# Revit family: Gira_220303
name_source: partatom
category: Elektroinstallationen
revit_build: Autodesk Revit 2017 (Build: 20160225_1515(x64)
units: mm (PartAtom-declared; Revit-internal decimal feet)

## family parameters
Basisbauteil = Fläche
Beim Laden mit Abzugskörper schneiden = Nein
Bemaßung runder Anschluss = Durchmesser verwenden
Beschriftungsausrichtung beibehalten = Nein
Gemeinsam genutzt = Nein
Raumberechnungspunkt = Nein
Teiletyp = Normal

## types (2) — shared parameters
Acoustic signal = Ja
Analogue input = Nein
BIM = https://media.stage.bim.site und Tasten.rfa
Beschreibung = Rock.set 3g insc. Sys55 PWl,Rocker set, 3-gang inscribable,System 55,pure white glossy (lacquered),Notes :,- Inscribable rocker sets and rocker sets with inscription space can be provided with a customised inscription. The order is processed by the wholesaler specified during the rockers' order process.,- Inscribable rocker sets and rocker sets without inscription space are made of metal, which can lead to impairments to the range in wireless applications.,- This product can only be ordered via the Gira Inscription Service.,- Professional labelling with the Gira Inscription Service www.marking.gira.com.
Bus connection included = Nein
Bus system KNX = Ja
Bus system KNX radio = Nein
Bus system LON = Nein
Bus system Powernet = Nein
Bus system radio frequent = Nein
Colour = White
Data sheet = https://katalog.gira.de
Degree of protection (IP) = IP20
GTIN = 4010337012443
HAN = 220303
Halogen free = Ja
Hersteller = Gira
Imprint/indication = Without imprint
Material = Other
Material quality = Other
Model = Single rocker
Monitoring window/light outlet = Ja
Mounting method = Flush mounted (plaster)
Number of channels = 3
Other bus systems = None
Productwebsite = http://katalog.gira.de
RAL-number (akin) = 9010
Scannable symbol / barrier free = Nein
Suitable for degree of protection (IP) = IP20
Suitable for touch sensor connector for bus system = Nein
Surface finishing = Not applicable
Surface protection = Other
Transparent = Nein
Type of fastening = Clamp mounting
Typname = Rocker set 3-g inscr. System 55 p.white(lac.)
URL = https://www.gira.de
Utilization = Switch/push button
Vorgabe-Ansicht = 1219 mm
Weather station = Nein
With DCF77 = Nein
With exchangeable lens/symbol = Nein
With heating = Nein
With label area = Nein

## type names (no varying parameters)
- Rocker set 3-g in.sp. System 55 clear/p.white
- Sys55_Abdeckung_Schalten und Tasten

## geometry (parser evidence)
native form markers: Sweep x7
no freeform markers — native parametric forms only
